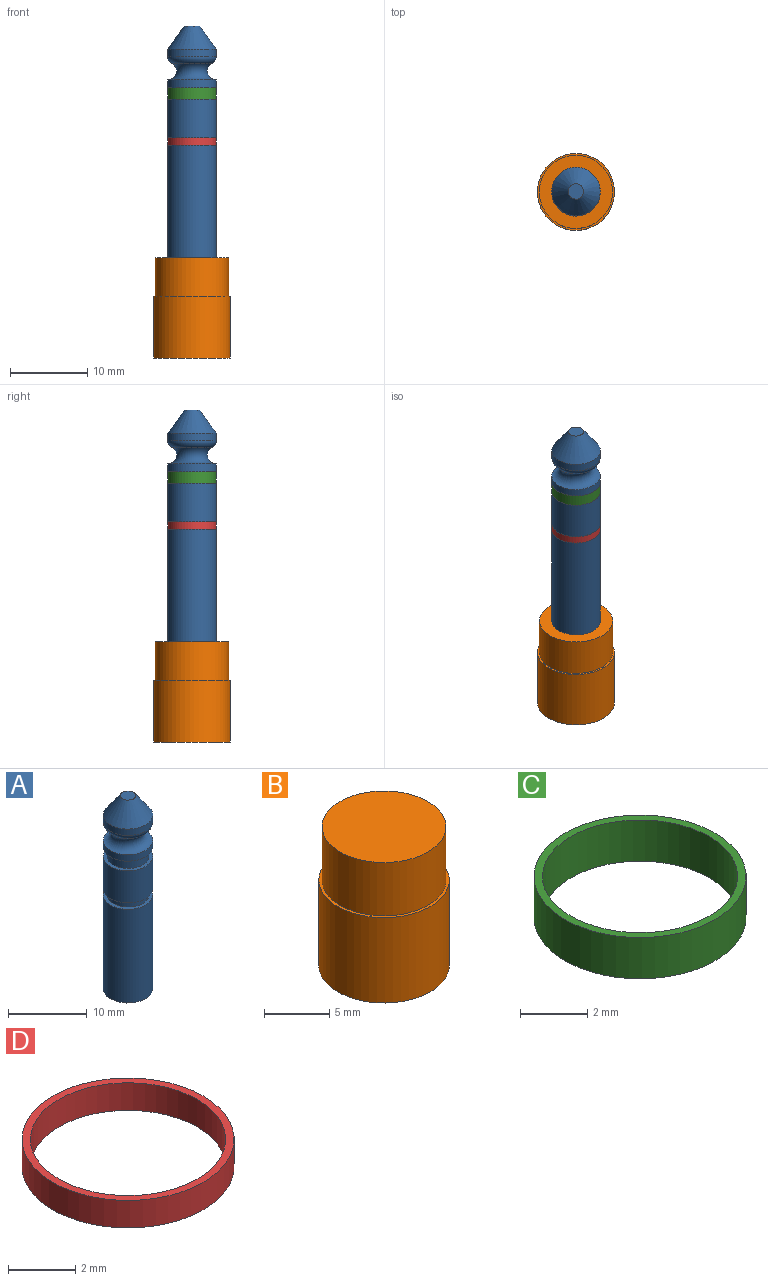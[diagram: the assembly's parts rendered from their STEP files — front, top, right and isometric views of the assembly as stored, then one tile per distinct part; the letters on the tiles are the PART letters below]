
ASSEMBLY  parts=4 mates=3
PART A: 15 faces, bbox 6.8x6.8x30.1 mm
  f0: plane 6.3x6.3mm, normal (0,0,-1), area 31.2mm2, adj f1
  f1: cylinder r=3.15mm len=14.6mm, axis (0,0,-1), area 289mm2, adj f0,f2
  f2: plane 6.3x6.3mm, normal (0,0,1), area 9.1mm2, adj f1,f3
  f3: cylinder r=2.65mm len=5.3mm, axis (0,0,-1), area 16.7mm2, adj f2,f4
  f4: plane 6.3x6.3mm, normal (0,0,-1), area 9.1mm2, adj f3,f5
  f5: cylinder r=3.15mm len=6.3mm, axis (0,0,-1), area 99mm2, adj f4,f6
  f6: plane 6.3x6.3mm, normal (0,0,1), area 9.1mm2, adj f5,f7
  f7: cylinder r=2.65mm len=5.3mm, axis (0,0,-1), area 25mm2, adj f6,f8
  f8: plane 6.3x6.3mm, normal (0,0,-1), area 9.1mm2, adj f7,f9
  f9: cylinder r=3.15mm len=6.3mm, axis (0,0,-1), area 19.8mm2, adj f8,f10
  f10: torus R=3.15mm, axis (0,0,-1), area 45.3mm2, adj f9,f11
  f11: torus R=2.24mm, axis (0,0,-1), area 19mm2, adj f10,f12
  f12: cylinder r=3.15mm len=6.3mm, axis (0,0,-1), area 19.8mm2, adj f11,f13
  f13: cone r=1mm half-angle=35.6deg, axis (0,0,-1), area 48.1mm2, adj f12,f14
  f14: plane 2x2mm, normal (0,0,1), area 3.1mm2, adj f13
PART B: 5 faces, bbox 10x10x13 mm
  f0: cylinder r=5mm len=10mm, axis (0,0,-1), area 251.3mm2, adj f1,f2
  f1: plane 10x10mm, normal (0,0,1), area 7.7mm2, adj f0,f3
  f2: plane 10x10mm, normal (0,0,-1), area 78.5mm2, adj f0
  f3: cylinder r=4.75mm len=9.5mm, axis (0,0,-1), area 149.2mm2, adj f1,f4
  f4: plane 9.5x9.5mm, normal (0,0,1), area 70.9mm2, adj f3
PART C: 4 faces, bbox 6.3x6.3x1.5 mm
  f0: cylinder r=2.9mm len=5.8mm, axis (0,0,-1), area 27.3mm2, adj f2,f3
  f1: cylinder r=3.15mm len=6.3mm, axis (0,0,-1), area 29.7mm2, adj f2,f3
  f2: plane 6.3x6.3mm, normal (0,0,1), area 4.8mm2, adj f0,f1
  f3: plane 6.3x6.3mm, normal (0,0,-1), area 4.8mm2, adj f0,f1
PART D: 4 faces, bbox 6.3x6.3x1 mm
  f0: cylinder r=2.9mm len=5.8mm, axis (0,0,-1), area 18.2mm2, adj f2,f3
  f1: cylinder r=3.15mm len=6.3mm, axis (0,0,-1), area 19.8mm2, adj f2,f3
  f2: plane 6.3x6.3mm, normal (0,0,1), area 4.8mm2, adj f0,f1
  f3: plane 6.3x6.3mm, normal (0,0,-1), area 4.8mm2, adj f0,f1
PLACE A t=(0,0,-11.64)mm
PLACE B t=(0,0,-24.64)mm fixed
PLACE C t=(0,0,8.96)mm
PLACE D t=(0,0,2.96)mm
MATE fastened A.f1 <-> B.f3  axis (0,0,-1) through (0,0,-11.64)mm
MATE fastened A.f1 <-> D.f1  axis (0,0,-1) through (0,0,3.46)mm
MATE fastened C.f1 <-> A.f1  axis (0,0,-1) through (0,0,8.96)mm
